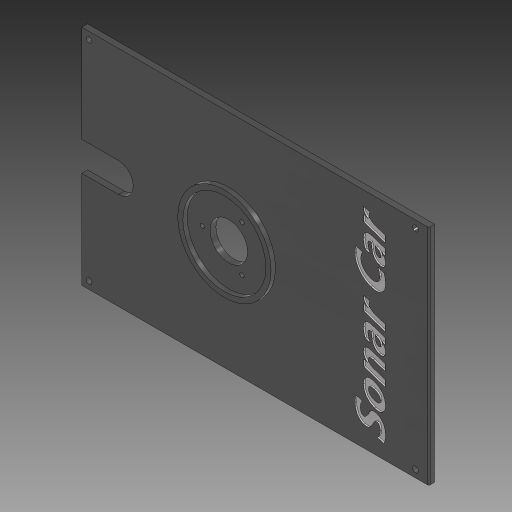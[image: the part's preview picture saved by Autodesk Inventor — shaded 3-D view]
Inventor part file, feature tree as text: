
AUTODESK INVENTOR PART (.ipt)
format: ipt  version: 2023 (Build 270158000, 158)  size: 861,696 bytes
history: native  units: mm
features: sketch x6, extrude x5, other x2, fillet x1
ambient origin geometry x8: Origin, YZ Plane, XZ Plane, XY Plane, X Axis, Y Axis, Z Axis, Center Point
bodies: Body1 (feature_tree)
feature tree (14):
  other  "Těleso1"
  extrude  "Vysunutí1"  Depth=120.0mm
  extrude  "Vysunutí2"  Depth=80.0mm
  extrude  "Vysunutí3"  Depth=2.0mm
  extrude  "Vysunutí4"  Depth=20.0mm
  extrude  "Vysunutí5"  Depth=20.0mm
  other  "Reliéf1"
  fillet  "Zaoblení2"  Radius=2.0mm
  sketch  "Náčrt1"
  sketch  "Náčrt2"
  sketch  "Náčrt3"
  sketch  "Náčrt4"
  sketch  "Náčrt5"
  sketch  "Náčrt6"
